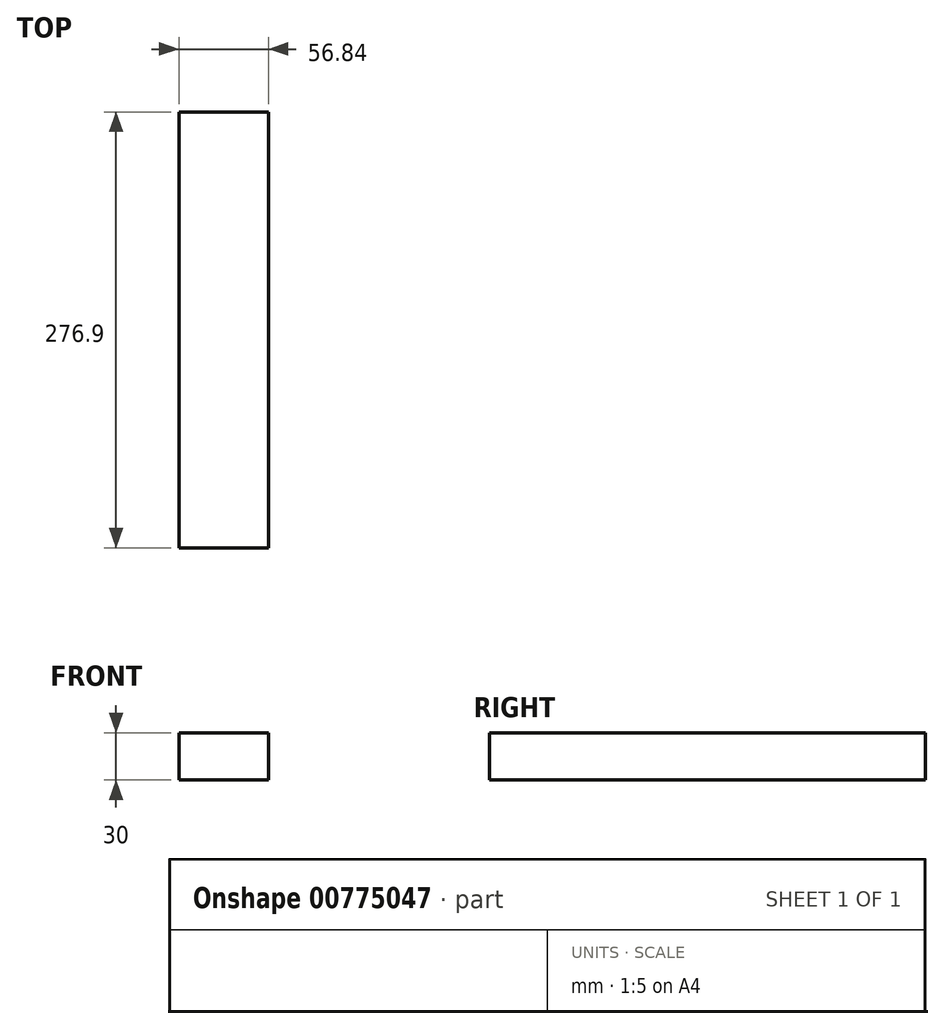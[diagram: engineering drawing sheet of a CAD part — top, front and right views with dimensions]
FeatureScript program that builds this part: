
annotation { "Feature Type Name" : "Feature", "Feature Type Description" : "" }
export const myFeature = defineFeature(function(context is Context, id is Id, definition is map)
    precondition{}
    {
        {
            var Q0;
            Q0=qCreatedBy(makeId("Top.planeOp"),FACE);
            var sketch = newSketch(context, id + "F0", { "sketchPlane" : qUnion([Q0])});
            skLineSegment(sketch, "E0.bottom", {"start": v(0, 0) * mm, "end": v(56.84, 0) * mm});
            skLineSegment(sketch, "E0.top", {"start": v(0, 276.9) * mm, "end": v(56.84, 276.9) * mm});
            skLineSegment(sketch, "E0.left", {"start": v(0, 0) * mm, "end": v(0, 276.9) * mm});
            skLineSegment(sketch, "E0.right", {"start": v(56.84, 0) * mm, "end": v(56.84, 276.9) * mm});
            skSolve(sketch);
        }
        {
            var Q0;
            Q0=makeQuery(id+"F0.imprint","IMPRINT",FACE,{"disambiguationData":[TD([[makeQuery(id+"F0.imprint","IMPRINT",EDGE,{"derivedFrom":sQuery(id+"F0.wireOp",EDGE,"E0.bottom")}),1.0]])]});
            extrude(context, id + "F1", {"entities" : qUnion([Q0]), "depth" : 30 * mm, "offsetDistance" : 25 * mm});
        }
    });
